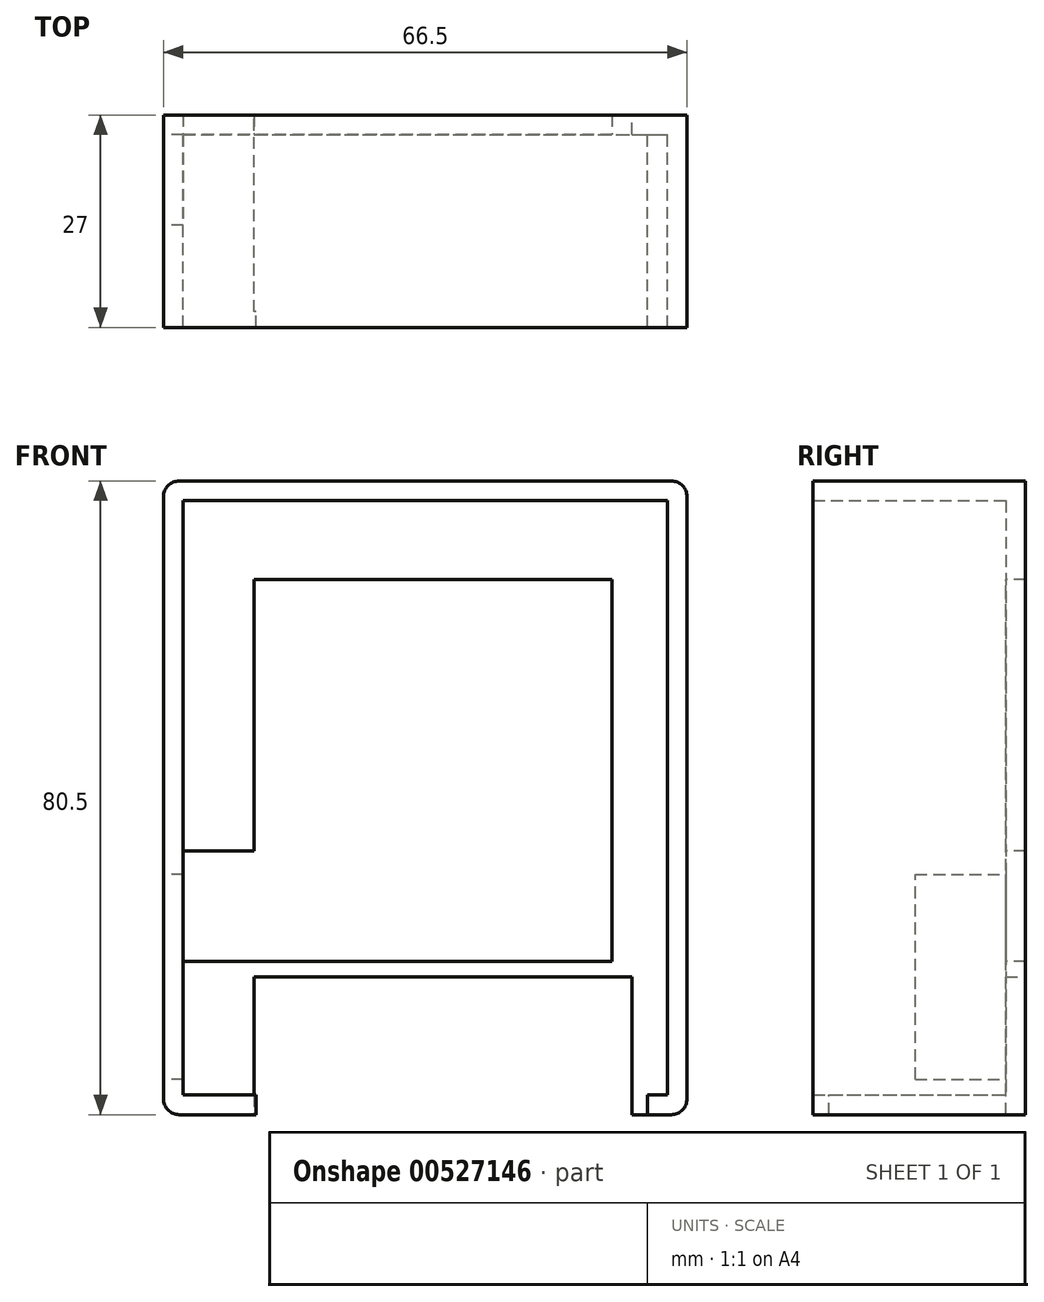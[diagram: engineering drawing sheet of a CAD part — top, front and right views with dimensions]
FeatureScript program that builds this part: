
annotation { "Feature Type Name" : "Feature", "Feature Type Description" : "" }
export const myFeature = defineFeature(function(context is Context, id is Id, definition is map)
    precondition{}
    {
        {
            var Q0;
            Q0=qCreatedBy(makeId("Front.planeOp"),FACE);
            var sketch = newSketch(context, id + "F0", { "sketchPlane" : qUnion([Q0])});
            skLineSegment(sketch, "E0.bottom", {"start": v(-2.5, 78) * mm, "end": v(64, 78) * mm});
            skLineSegment(sketch, "E0.top", {"start": v(-2.5, -2.5) * mm, "end": v(64, -2.5) * mm});
            skLineSegment(sketch, "E0.left", {"start": v(-2.5, 78) * mm, "end": v(-2.5, -2.5) * mm});
            skLineSegment(sketch, "E0.right", {"start": v(64, 78) * mm, "end": v(64, -2.5) * mm});
            skSolve(sketch);
        }
        {
            var Q0;
            Q0 = qSketchRegion(id + "F0", true);
            var Q1;
            Q1=makeQuery(id+"F0.imprint","IMPRINT",FACE,{"disambiguationData":[TD([[makeQuery(id+"F0.imprint","IMPRINT",EDGE,{"derivedFrom":sQuery(id+"F0.wireOp",EDGE,"E0.bottom")}),-1.0]])]});
            extrude(context, id + "F1", {"entities" : qUnion([Q0, Q1]), "depth" : 27 * mm, "offsetDistance" : 25 * mm});
        }
        {
            var Q0;
            Q0=makeQuery(id+"F1.opExtrude","CAP_FACE",FACE,{"disambiguationData":[OSD([sQuery(id+"F0.wireOp",EDGE,"E0.bottom"),sQuery(id+"F0.wireOp",EDGE,"E0.top"),sQuery(id+"F0.wireOp",EDGE,"E0.left"),sQuery(id+"F0.wireOp",EDGE,"E0.right")])],"isStart":false});
            shell(context, id + "F2", {"entities" : qUnion([Q0]), "thickness" : 2.5 * mm});
        }
        {
            var Q0;
            Q0=makeQuery(id+"F1.opExtrude","SWEPT_EDGE",EDGE,{"disambiguationData":[OSD([sQuery(id+"F0.wireOp",EDGE,"E0.bottom"),sQuery(id+"F0.wireOp",EDGE,"E0.right")])]});
            var Q1;
            Q1=makeQuery(id+"F1.opExtrude","SWEPT_EDGE",EDGE,{"disambiguationData":[OSD([sQuery(id+"F0.wireOp",EDGE,"E0.bottom"),sQuery(id+"F0.wireOp",EDGE,"E0.left")])]});
            var Q2;
            Q2=makeQuery(id+"F1.opExtrude","SWEPT_EDGE",EDGE,{"disambiguationData":[OSD([sQuery(id+"F0.wireOp",EDGE,"E0.top"),sQuery(id+"F0.wireOp",EDGE,"E0.right")])]});
            var Q3;
            Q3=makeQuery(id+"F1.opExtrude","SWEPT_EDGE",EDGE,{"disambiguationData":[OSD([sQuery(id+"F0.wireOp",EDGE,"E0.top"),sQuery(id+"F0.wireOp",EDGE,"E0.left")])]});
            fillet(context, id + "F3", {"entities" : qUnion([Q0, Q1, Q2, Q3]), "radius" : 2 * mm, "tangentPropagation" : true, "allowEdgeOverflow" : false});
        }
        {
            var Q0;
            Q0=makeQuery(id+"F2.opShell","OFFSET_FACE",FACE,{"disambiguationData":[OSD([sQuery(id+"F0.wireOp",EDGE,"E0.top")])]});
            var sketch = newSketch(context, id + "F4", { "sketchPlane" : qUnion([Q0])});
            skLineSegment(sketch, "E1.bottom", {"start": v(59, -27) * mm, "end": v(9.25, -27) * mm});
            skLineSegment(sketch, "E1.top", {"start": v(59, -2.5) * mm, "end": v(9.25, -2.5) * mm});
            skLineSegment(sketch, "E1.left", {"start": v(59, -27) * mm, "end": v(59, -2.5) * mm});
            skLineSegment(sketch, "E1.right", {"start": v(9.25, -27) * mm, "end": v(9.25, -2.5) * mm});
            skSolve(sketch);
        }
        {
            var Q0;
            Q0 = qSketchRegion(id + "F4", true);
            extrude(context, id + "F5", {"entities" : qUnion([Q0]), "operationType" : NewBodyOperationType.REMOVE, "oppositeDirection" : true, "depth" : 25 * mm, "offsetDistance" : 25 * mm});
        }
        {
            var Q0;
            Q0=makeQuery(id+"F2.opShell","OFFSET_FACE",FACE,{"disambiguationData":[OSD([sQuery(id+"F0.wireOp",EDGE,"E0.bottom"),sQuery(id+"F0.wireOp",EDGE,"E0.top"),sQuery(id+"F0.wireOp",EDGE,"E0.left"),sQuery(id+"F0.wireOp",EDGE,"E0.right")])]});
            var sketch = newSketch(context, id + "F6", { "sketchPlane" : qUnion([Q0])});
            skLineSegment(sketch, "E2.bottom", {"start": v(54.5, 17) * mm, "end": v(9, 17) * mm});
            skLineSegment(sketch, "E2.top", {"start": v(54.5, 65.5) * mm, "end": v(9, 65.5) * mm});
            skLineSegment(sketch, "E2.left", {"start": v(54.5, 17) * mm, "end": v(54.5, 65.5) * mm});
            skLineSegment(sketch, "E2.right", {"start": v(9, 17) * mm, "end": v(9, 65.5) * mm});
            skSolve(sketch);
        }
        {
            var Q0;
            Q0 = qSketchRegion(id + "F6", true);
            extrude(context, id + "F7", {"entities" : qUnion([Q0]), "operationType" : NewBodyOperationType.REMOVE, "oppositeDirection" : true, "depth" : 25 * mm, "offsetDistance" : 25 * mm});
        }
        {
            var Q0;
            Q0=makeQuery(id+"F1.opExtrude","CAP_FACE",FACE,{"disambiguationData":[OSD([sQuery(id+"F0.wireOp",EDGE,"E0.bottom"),sQuery(id+"F0.wireOp",EDGE,"E0.top"),sQuery(id+"F0.wireOp",EDGE,"E0.left"),sQuery(id+"F0.wireOp",EDGE,"E0.right")])],"isStart":true});
            var sketch = newSketch(context, id + "F8", { "sketchPlane" : qUnion([Q0])});
            skLineSegment(sketch, "E3.bottom", {"start": v(-57, 15) * mm, "end": v(-9, 15) * mm});
            skLineSegment(sketch, "E3.top", {"start": v(-57, -2.5) * mm, "end": v(-9, -2.5) * mm});
            skLineSegment(sketch, "E3.left", {"start": v(-57, 15) * mm, "end": v(-57, -2.5) * mm});
            skLineSegment(sketch, "E3.right", {"start": v(-9, 15) * mm, "end": v(-9, -2.5) * mm});
            skSolve(sketch);
        }
        {
            var Q0;
            Q0 = qSketchRegion(id + "F8", true);
            extrude(context, id + "F9", {"entities" : qUnion([Q0]), "operationType" : NewBodyOperationType.REMOVE, "oppositeDirection" : true, "depth" : 25 * mm, "offsetDistance" : 25 * mm});
        }
        {
            var Q0;
            Q0=makeQuery(id+"F1.opExtrude","SWEPT_FACE",FACE,{"disambiguationData":[OSD([sQuery(id+"F0.wireOp",EDGE,"E0.left")])]});
            var sketch = newSketch(context, id + "F10", { "sketchPlane" : qUnion([Q0])});
            skLineSegment(sketch, "E4.bottom", {"start": v(14, 2) * mm, "end": v(2.5, 2) * mm});
            skLineSegment(sketch, "E4.top", {"start": v(14, 28) * mm, "end": v(2.5, 28) * mm});
            skLineSegment(sketch, "E4.left", {"start": v(14, 2) * mm, "end": v(14, 28) * mm});
            skLineSegment(sketch, "E4.right", {"start": v(2.5, 2) * mm, "end": v(2.5, 28) * mm});
            skSolve(sketch);
        }
        {
            var Q0;
            Q0 = qSketchRegion(id + "F10", true);
            extrude(context, id + "F11", {"entities" : qUnion([Q0]), "operationType" : NewBodyOperationType.REMOVE, "oppositeDirection" : true, "depth" : 25 * mm, "offsetDistance" : 25 * mm});
        }
        {
            var Q0;
            Q0=makeQuery(id+"F11.boolean.opBoolean","MERGE",FACE,{"derivedFrom":[makeQuery(id+"F5.boolean.opBoolean","MERGE",FACE,{"derivedFrom":[makeQuery(id+"F2.opShell","OFFSET_FACE",FACE,{"disambiguationData":[OSD([sQuery(id+"F0.wireOp",EDGE,"E0.bottom"),sQuery(id+"F0.wireOp",EDGE,"E0.top"),sQuery(id+"F0.wireOp",EDGE,"E0.left"),sQuery(id+"F0.wireOp",EDGE,"E0.right")])]}),makeQuery(id+"F5.opExtrude","SWEPT_FACE",FACE,{"disambiguationData":[OSD([sQuery(id+"F4.wireOp",EDGE,"E1.top")])]})]}),makeQuery(id+"F11.opExtrude","SWEPT_FACE",FACE,{"disambiguationData":[OSD([sQuery(id+"F10.wireOp",EDGE,"E4.right")])]})]});
            var sketch = newSketch(context, id + "F12", { "sketchPlane" : qUnion([Q0])});
            skLineSegment(sketch, "E5.bottom", {"start": v(9, 17) * mm, "end": v(0, 17) * mm});
            skLineSegment(sketch, "E5.top", {"start": v(9, 31) * mm, "end": v(0, 31) * mm});
            skLineSegment(sketch, "E5.left", {"start": v(9, 17) * mm, "end": v(9, 31) * mm});
            skLineSegment(sketch, "E5.right", {"start": v(0, 17) * mm, "end": v(0, 31) * mm});
            skSolve(sketch);
        }
        {
            var Q0;
            Q0 = qSketchRegion(id + "F12", true);
            extrude(context, id + "F13", {"entities" : qUnion([Q0]), "operationType" : NewBodyOperationType.REMOVE, "oppositeDirection" : true, "depth" : 25 * mm, "offsetDistance" : 25 * mm});
        }
    });
